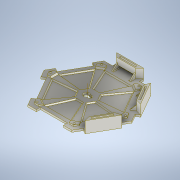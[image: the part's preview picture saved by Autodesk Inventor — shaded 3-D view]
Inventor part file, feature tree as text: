
AUTODESK INVENTOR PART (.ipt)
format: ipt  version: 2020 (Build 240168000, 168)  size: 926,720 bytes
history: native  units: mm
features: chamfer x9, extrude x8, sketch x2, pattern_circular x2, fillet x1
ambient origin geometry x8: Origin, YZ Plane, XZ Plane, XY Plane, X Axis, Y Axis, Z Axis, Center Point
bodies: Body1 (feature_tree)
feature tree (22):
  sketch  "Sketch6"  dims[d72=6.5mm d87=15.0mm]
  extrude  "Plate"  Depth=15.0mm
  extrude  "Cazzetti"  Depth=2.5mm
  extrude  "ScavoStrip"  Depth=2.5mm
  extrude  "ScalinoAllineamento"  Depth=2.5mm
  extrude  "Foro"  Depth=2.5mm
  extrude  "ForoMuro"  TaperAngle=0.0deg  [1 undecoded]
  extrude  "Scavi"  Depth=2.5mm
  chamfer  "Smussi"  Distance=3.0mm
  pattern_circular  "ScalinoCircolare"  [2 undecoded]
  chamfer  "Chamfer3"  Distance=15.0mm
  chamfer  "Chamfer4"  Distance=2.0mm
  chamfer  "Chamfer5"  Distance=13.0mm
  chamfer  "Chamfer6"  Distance=2.5mm
  chamfer  "Chamfer7"  Distance=26.0mm
  chamfer  "Chamfer8"  Distance=70.0mm
  extrude  "Nervature"  Depth=2.5mm
  chamfer  "SmussoNervature"  Distance=1.25mm
  pattern_circular  "Circular Pattern2"  [2 undecoded]
  fillet  "Raccordo"  Radius=5.0mm
  chamfer  "ForoSmusso"  Distance=2.0mm
  sketch  "Sketch10"  dims[d88=6.5mm d92=2.5mm d95=1.25mm d96=25.0mm d98=25.0mm d100=0.0mm d105=30.0mm d106=3.0mm d107=0.0mm d108=6.5mm d112=15.0mm d113=2.0mm d114=13.0mm d115=2.5mm d116=26.0mm d118=70.0mm d119=54.121778mm d120=1.25mm d121=15.0mm d122=0.0mm d125=5.0mm d126=0.0mm d127=2.0mm d130=7.0mm d131=2.0mm d132=0.0mm d133=60.0mm d134=360.0deg d136=4.0mm d138=3.0mm d139=3.0mm d140=9.25mm d141=0.0mm d142=20.0mm d143=30.0mm d145=3.5mm d146=4.0mm d147=10.0mm d148=0.0mm d149=7.0mm d150=2.5mm d152=6.4mm d154=6.4mm d155=30.0mm d157=120.0deg d159=60.0mm d161=360.0deg d163=2.0mm d164=2.0mm d165=45.0deg d166=1.5mm d167=0.0mm d171=1.5mm d172=2.0mm d173=45.0deg d174=1.5mm d175=2.0mm d176=45.0deg d177=1.5mm d178=2.0mm d179=45.0deg d180=1.5mm d181=2.0mm d182=45.0deg d183=1.5mm d184=2.0mm d185=45.0deg d186=1.5mm d187=2.0mm d188=45.0deg d189=2.0mm d190=8.0mm d191=8.0mm d192=0.0mm d193=8.0mm d194=2.0mm d195=45.0deg d196=30.0mm d197=120.0deg d199=1.0mm d200=1.0mm d201=2.0mm d202=45.0deg d205=6.6mm d128=0.872665mm d160=0.872665mm d162=0.872665mm]
note: 5 required parameter values undecoded (feature->parameter linkage not recoverable at this tier; creation-order binding heuristic only, values carry confidence <= 0.55)
